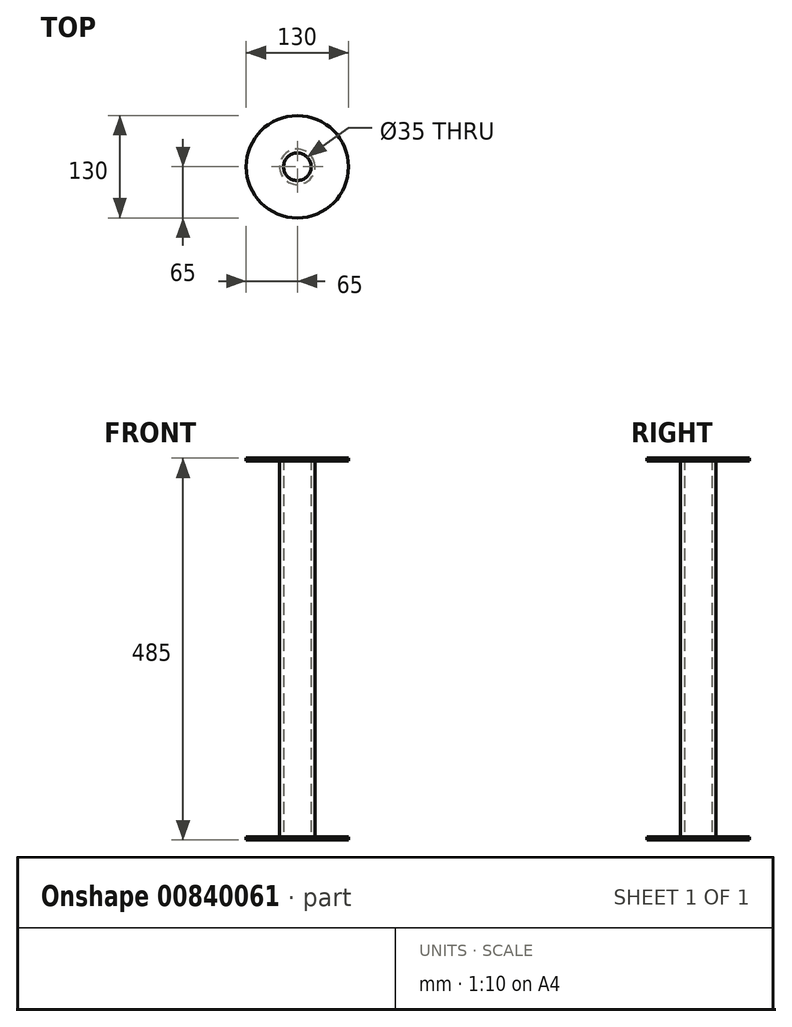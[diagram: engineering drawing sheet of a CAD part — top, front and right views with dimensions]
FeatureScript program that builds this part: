
annotation { "Feature Type Name" : "Feature", "Feature Type Description" : "" }
export const myFeature = defineFeature(function(context is Context, id is Id, definition is map)
    precondition{}
    {
        {
            var Q0;
            Q0=qCreatedBy(makeId("Front.planeOp"),FACE);
            var sketch = newSketch(context, id + "F0", { "sketchPlane" : qUnion([Q0])});
            skLineSegment(sketch, "E0", {"start": v(-17.5, 242.5) * mm, "end": v(-65, 242.5) * mm});
            skLineSegment(sketch, "E1", {"start": v(-65, 242.5) * mm, "end": v(-65, 238.5) * mm});
            skLineSegment(sketch, "E2", {"start": v(-65, 238.5) * mm, "end": v(-22.5, 238.5) * mm});
            skLineSegment(sketch, "E3", {"start": v(-22.5, 238.5) * mm, "end": v(-22.5, 0) * mm});
            skLineSegment(sketch, "E4", {"start": v(-17.5, 0) * mm, "end": v(-17.5, 242.5) * mm});
            skLineSegment(sketch, "E5.MirrorCS", {"start": v(-22.5, -238.5) * mm, "end": v(-22.5, 0) * mm});
            skLineSegment(sketch, "E6.MirrorCS", {"start": v(-17.5, 0) * mm, "end": v(-17.5, -242.5) * mm});
            skLineSegment(sketch, "E7.MirrorCS", {"start": v(-65, -238.5) * mm, "end": v(-22.5, -238.5) * mm});
            skLineSegment(sketch, "E8.MirrorCS", {"start": v(-17.5, -242.5) * mm, "end": v(-65, -242.5) * mm});
            skLineSegment(sketch, "E9.MirrorCS", {"start": v(-65, -242.5) * mm, "end": v(-65, -238.5) * mm});
            skLineSegment(sketch, "E10", {"start": v(0, 0) * mm, "end": v(0, 72.77) * mm, "construction": true});
            skSolve(sketch);
        }
        {
            var Q0;
            Q0=makeQuery(id+"F0.imprint","IMPRINT",FACE,{"disambiguationData":[TD([[makeQuery(id+"F0.imprint","IMPRINT",EDGE,{"derivedFrom":sQuery(id+"F0.wireOp",EDGE,"E0")}),1.0]])]});
            var Q1;
            Q1=sQuery(id+"F0.wireOp",EDGE,"E10");
            revolve(context, id + "F1", {"surfaceOperationType" : NewSurfaceOperationType.NEW, "entities" : qUnion([Q0]), "axis" : qUnion([Q1]), "revolveType" : RevolveType.FULL});
        }
    });
